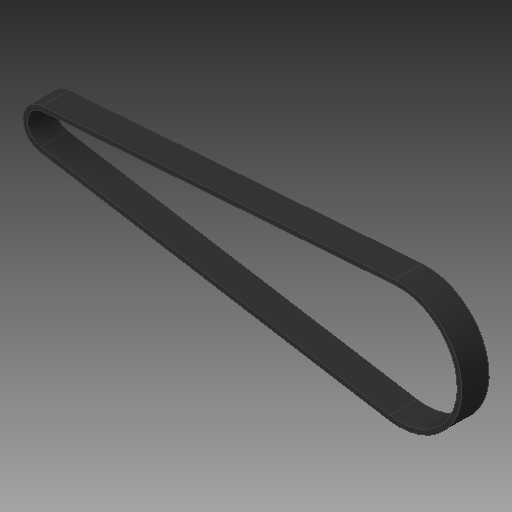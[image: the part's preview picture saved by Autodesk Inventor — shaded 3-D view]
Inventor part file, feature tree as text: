
AUTODESK INVENTOR PART (.ipt)
format: ipt  version: 2018.2 (Build 222227000, 227)  size: 109,056 bytes
history: native  units: mm
features: other x3, extrude x1, reference x1
ambient origin geometry x8: Origin, YZ Plane, XZ Plane, XY Plane, X Axis, Y Axis, Z Axis, Center Point
bodies: Body1 (feature_tree)
feature tree (5):
  extrude  "Extrusion2"  Depth=1.0mm
  reference  "Reference2"
  other  "<userpath>\OneDrive\Documents\2018 UBC\ELEC 391\Controller\CAD\Pok Mk3.iam"
  other  "Pok Mk3.iam"
  other  "GT2 Gear Big:1"
